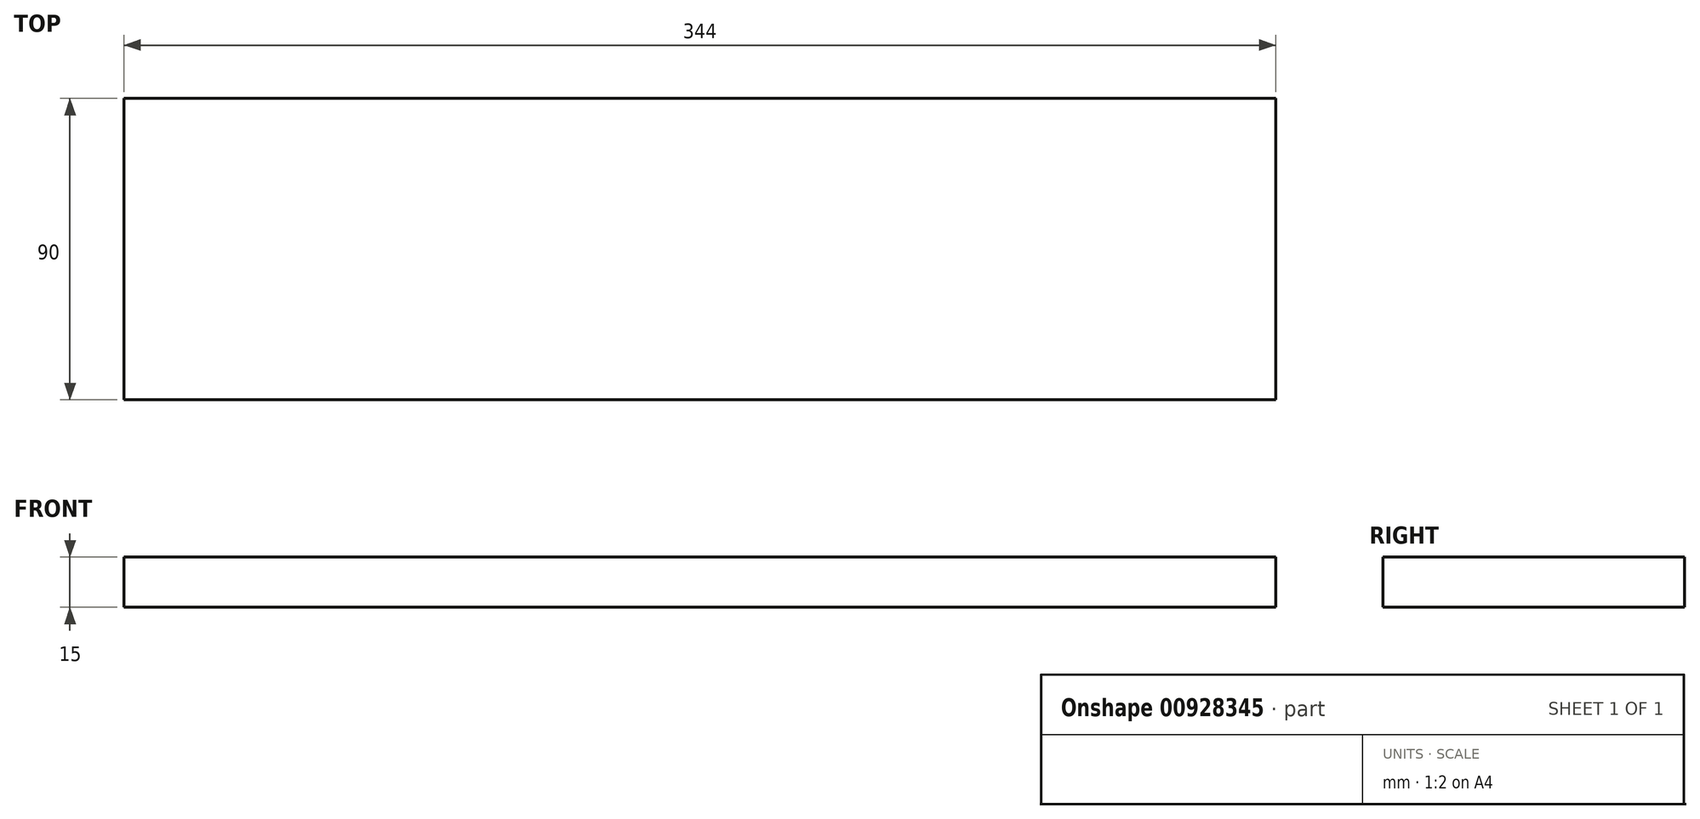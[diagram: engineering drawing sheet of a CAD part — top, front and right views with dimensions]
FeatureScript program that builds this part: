
annotation { "Feature Type Name" : "Feature", "Feature Type Description" : "" }
export const myFeature = defineFeature(function(context is Context, id is Id, definition is map)
    precondition{}
    {
        {
            var Q0;
            Q0=qCreatedBy(makeId("Top.planeOp"),FACE);
            var sketch = newSketch(context, id + "F0", { "sketchPlane" : qUnion([Q0])});
            skLineSegment(sketch, "E0.bottom", {"start": v(172, 45) * mm, "end": v(-172, 45) * mm});
            skLineSegment(sketch, "E0.top", {"start": v(172, -45) * mm, "end": v(-172, -45) * mm});
            skLineSegment(sketch, "E0.left", {"start": v(172, 45) * mm, "end": v(172, -45) * mm});
            skLineSegment(sketch, "E0.right", {"start": v(-172, 45) * mm, "end": v(-172, -45) * mm});
            skPoint(sketch, "E0.middle", {"position": v(0, 0) * mm});
            skSolve(sketch);
        }
        {
            var Q0;
            Q0=makeQuery(id+"F0.imprint","IMPRINT",FACE,{"disambiguationData":[TD([[makeQuery(id+"F0.imprint","IMPRINT",EDGE,{"derivedFrom":sQuery(id+"F0.wireOp",EDGE,"E0.bottom")}),1.0]])]});
            extrude(context, id + "F1", {"entities" : qUnion([Q0]), "depth" : 15 * mm, "offsetDistance" : 25 * mm});
        }
    });
